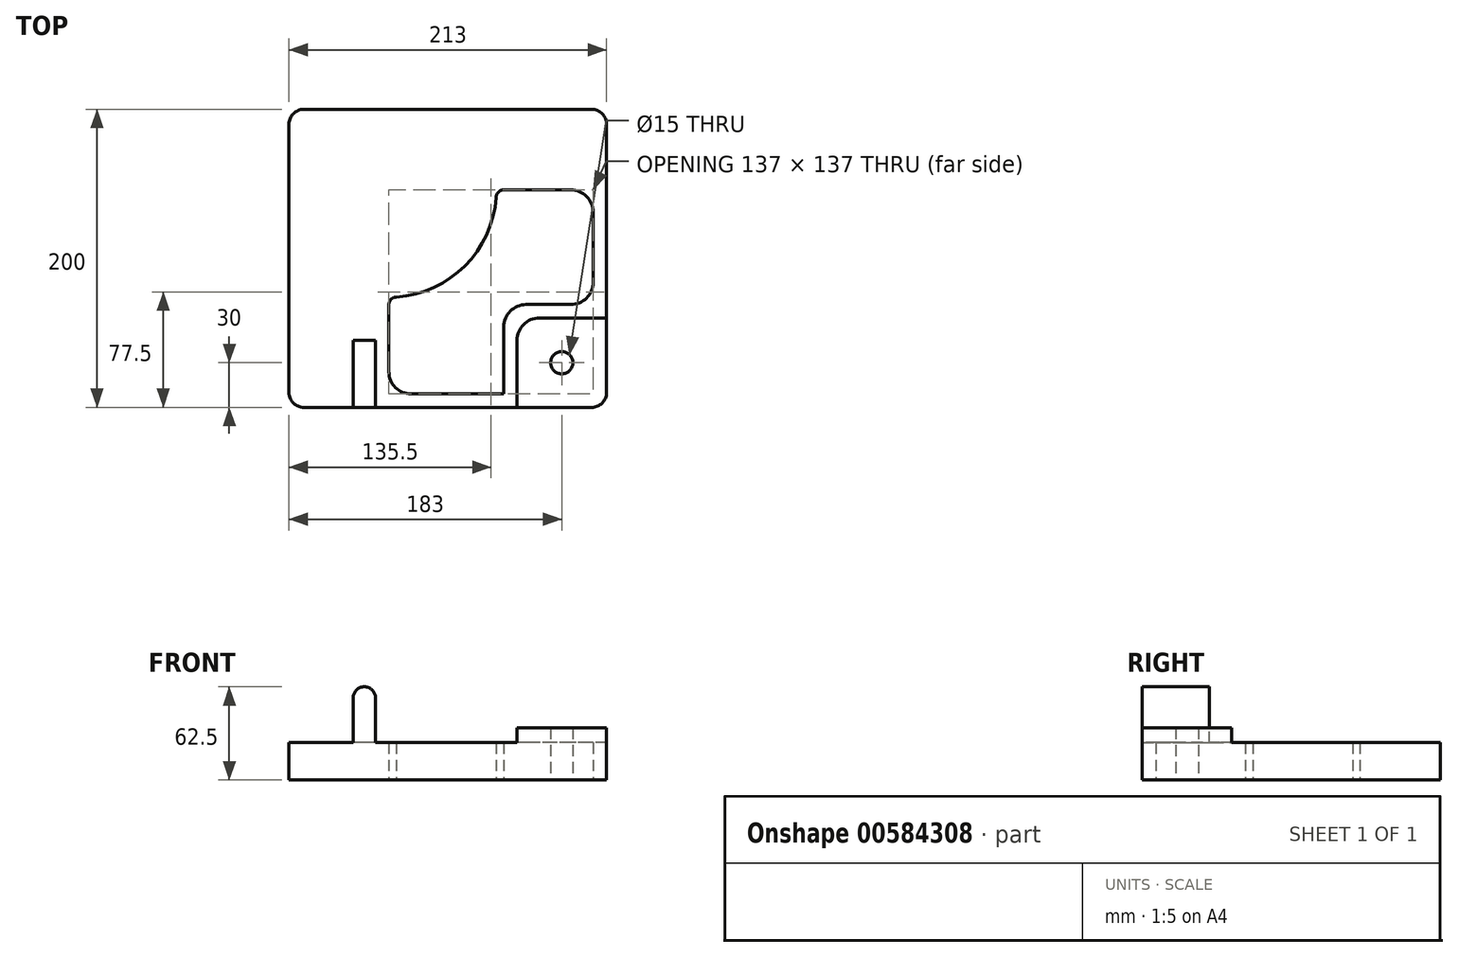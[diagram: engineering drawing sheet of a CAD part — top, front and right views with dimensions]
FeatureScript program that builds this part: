
annotation { "Feature Type Name" : "Feature", "Feature Type Description" : "" }
export const myFeature = defineFeature(function(context is Context, id is Id, definition is map)
    precondition{}
    {
        {
            var Q0;
            Q0=qCreatedBy(makeId("Top.planeOp"),FACE);
            var sketch = newSketch(context, id + "F0", { "sketchPlane" : qUnion([Q0])});
            skLineSegment(sketch, "E0.bottom", {"start": v(106.5, 100) * mm, "end": v(-106.5, 100) * mm});
            skLineSegment(sketch, "E0.top", {"start": v(106.5, -100) * mm, "end": v(-106.5, -100) * mm});
            skLineSegment(sketch, "E0.left", {"start": v(106.5, 100) * mm, "end": v(106.5, -100) * mm});
            skLineSegment(sketch, "E0.right", {"start": v(-106.5, 100) * mm, "end": v(-106.5, -100) * mm});
            skPoint(sketch, "E0.middle", {"position": v(0, 0) * mm});
            skLineSegment(sketch, "E1", {"start": v(106.5, -100) * mm, "end": v(-39.5, -100) * mm, "construction": true});
            skLineSegment(sketch, "E2", {"start": v(-39.5, -100) * mm, "end": v(-39.5, -91) * mm, "construction": true});
            skLineSegment(sketch, "E3", {"start": v(106.5, -100) * mm, "end": v(46.5, -100) * mm, "construction": true});
            skLineSegment(sketch, "E4", {"start": v(46.5, -100) * mm, "end": v(46.5, -40) * mm, "construction": true});
            skLineSegment(sketch, "E5", {"start": v(46.5, -40) * mm, "end": v(106.5, -40) * mm, "construction": true});
            skLineSegment(sketch, "E6", {"start": v(106.5, -40) * mm, "end": v(106.5, -100) * mm, "construction": true});
            skLineSegment(sketch, "E7", {"start": v(46.5, -40) * mm, "end": v(37.5, -40) * mm, "construction": true});
            skLineSegment(sketch, "E8", {"start": v(46.5, -40) * mm, "end": v(46.5, 46) * mm, "construction": true});
            skLineSegment(sketch, "E9", {"start": v(97.5, 46) * mm, "end": v(97.5, -16) * mm});
            skLineSegment(sketch, "E10", {"start": v(37.5, -91) * mm, "end": v(37.5, -46) * mm});
            skLineSegment(sketch, "E11", {"start": v(82.5, -31) * mm, "end": v(52.5, -31) * mm});
            skArc(sketch, "E12", {"start": v(37.5, -46) * mm, "mid": v(41.9, -35.4) * mm, "end": v(52.5, -31) * mm});
            skLineSegment(sketch, "E13", {"start": v(-39.5, -91) * mm, "end": v(37.5, -91) * mm});
            skLineSegment(sketch, "E14", {"start": v(97.5, 46) * mm, "end": v(82.5, 46) * mm});
            skLineSegment(sketch, "E15", {"start": v(97.5, 46) * mm, "end": v(97.5, 31) * mm});
            skLineSegment(sketch, "E16", {"start": v(97.5, 31) * mm, "end": v(82.5, 31) * mm, "construction": true});
            skLineSegment(sketch, "E17", {"start": v(82.5, 31) * mm, "end": v(82.5, 46) * mm, "construction": true});
            skLineSegment(sketch, "E18", {"start": v(37.5, -91) * mm, "end": v(22.5, -91) * mm});
            skLineSegment(sketch, "E19", {"start": v(22.5, -91) * mm, "end": v(37.5, -91) * mm});
            skLineSegment(sketch, "E20", {"start": v(37.5, -76) * mm, "end": v(37.5, -91) * mm});
            skArc(sketch, "E21", {"start": v(97.5, 31) * mm, "mid": v(93.1, 41.6) * mm, "end": v(82.5, 46) * mm});
            skArc(sketch, "E22", {"start": v(82.5, -31) * mm, "mid": v(93.1, -26.6) * mm, "end": v(97.5, -16) * mm});
            skLineSegment(sketch, "E23", {"start": v(22.5, -91) * mm, "end": v(22.5, -76) * mm, "construction": true});
            skLineSegment(sketch, "E24", {"start": v(37.5, -76) * mm, "end": v(22.5, -76) * mm, "construction": true});
            skArc(sketch, "E25", {"start": v(22.5, -91) * mm, "mid": v(33.1, -86.6) * mm, "end": v(37.5, -76) * mm});
            skLineSegment(sketch, "E26", {"start": v(-24.5, -91) * mm, "end": v(-24.5, -76) * mm, "construction": true});
            skLineSegment(sketch, "E27", {"start": v(-24.5, -76) * mm, "end": v(-39.5, -76) * mm, "construction": true});
            skArc(sketch, "E28", {"start": v(-24.5, -91) * mm, "mid": v(-35.1, -86.6) * mm, "end": v(-39.5, -76) * mm});
            skLineSegment(sketch, "E29", {"start": v(37.5, -46) * mm, "end": v(52.5, -46) * mm, "construction": true});
            skLineSegment(sketch, "E30", {"start": v(97.5, -16) * mm, "end": v(106.5, -16) * mm, "construction": true});
            skLineSegment(sketch, "E31", {"start": v(37.5, -46) * mm, "end": v(37.5, -31) * mm, "construction": true});
            skLineSegment(sketch, "E32", {"start": v(52.5, -31) * mm, "end": v(37.5, -31) * mm, "construction": true});
            skLineSegment(sketch, "E33", {"start": v(82.5, -16) * mm, "end": v(97.5, -16) * mm, "construction": true});
            skLineSegment(sketch, "E34", {"start": v(97.5, -16) * mm, "end": v(97.5, -31) * mm, "construction": true});
            skLineSegment(sketch, "E35", {"start": v(97.5, -31) * mm, "end": v(82.5, -31) * mm, "construction": true});
            skLineSegment(sketch, "E36", {"start": v(82.5, -31) * mm, "end": v(82.5, -16) * mm, "construction": true});
            skPoint(sketch, "E37.endSnap0", {"position": v(90, 46) * mm});
            skLineSegment(sketch, "E38", {"start": v(-39.5, -76) * mm, "end": v(-39.5, -31) * mm});
            skLineSegment(sketch, "E39", {"start": v(-39.5, -31) * mm, "end": v(-34.5, -31) * mm, "construction": true});
            skLineSegment(sketch, "E40", {"start": v(-34.5, -31) * mm, "end": v(-34.5, -26) * mm, "construction": true});
            skLineSegment(sketch, "E41", {"start": v(-34.5, -26) * mm, "end": v(-39.5, -26) * mm, "construction": true});
            skLineSegment(sketch, "E42", {"start": v(-39.5, -26) * mm, "end": v(-39.5, -31) * mm, "construction": true});
            skLineSegment(sketch, "E43", {"start": v(82.5, 46) * mm, "end": v(37.5, 46) * mm});
            skLineSegment(sketch, "E44", {"start": v(37.5, 46) * mm, "end": v(32.5, 46) * mm, "construction": true});
            skLineSegment(sketch, "E45", {"start": v(32.5, 46) * mm, "end": v(32.5, 41) * mm, "construction": true});
            skLineSegment(sketch, "E46", {"start": v(32.5, 41) * mm, "end": v(37.5, 41) * mm, "construction": true});
            skLineSegment(sketch, "E47", {"start": v(37.5, 41) * mm, "end": v(37.5, 46) * mm, "construction": true});
            skArc(sketch, "E48", {"start": v(32.5, 41) * mm, "mid": v(33.96, 44.54) * mm, "end": v(37.5, 46) * mm});
            skArc(sketch, "E49", {"start": v(-34.5, -26) * mm, "mid": v(11.53, -5.03) * mm, "end": v(32.5, 41) * mm});
            skArc(sketch, "E50", {"start": v(-39.5, -31) * mm, "mid": v(-38.04, -27.46) * mm, "end": v(-34.5, -26) * mm});
            skSolve(sketch);
        }
        {
            var Q0;
            Q0 = qSketchRegion(id + "F0", true);
            var Q1;
            Q1=makeQuery(id+"F0.imprint","IMPRINT",FACE,{"disambiguationData":[TD([[makeQuery(id+"F0.imprint","IMPRINT",EDGE,{"derivedFrom":sQuery(id+"F0.wireOp",EDGE,"E19")}),1.0]])]});
            var Q2;
            Q2=makeQuery(id+"F0.imprint","IMPRINT",FACE,{"disambiguationData":[TD([[makeQuery(id+"F0.imprint","IMPRINT",EDGE,{"derivedFrom":sQuery(id+"F0.wireOp",EDGE,"E14")}),1.0]])]});
            var Q3;
            {var subQ0=sQuery(id+"F0.wireOp",EDGE,"E15");Q3=makeQuery(id+"F0.imprint","IMPRINT",FACE,{"disambiguationData":[TD([[makeQuery(id+"F0.imprint","IMPRINT",EDGE,{"derivedFrom":subQ0}),-1.0]])]});}
            extrude(context, id + "F1", {"entities" : qUnion([Q0, Q1, Q2, Q3]), "depth" : 25 * mm, "offsetDistance" : 25 * mm});
        }
        {
            var Q0;
            Q0=makeQuery(id+"F1.opExtrude","CAP_FACE",FACE,{"disambiguationData":[OSD([sQuery(id+"F0.wireOp",EDGE,"E0.bottom"),sQuery(id+"F0.wireOp",EDGE,"E0.top"),sQuery(id+"F0.wireOp",EDGE,"E0.left"),sQuery(id+"F0.wireOp",EDGE,"E0.right"),sQuery(id+"F0.wireOp",EDGE,"E9"),sQuery(id+"F0.wireOp",EDGE,"E10"),sQuery(id+"F0.wireOp",EDGE,"E11"),sQuery(id+"F0.wireOp",EDGE,"E12"),sQuery(id+"F0.wireOp",EDGE,"E13"),sQuery(id+"F0.wireOp",EDGE,"E21"),sQuery(id+"F0.wireOp",EDGE,"E22"),sQuery(id+"F0.wireOp",EDGE,"E25"),sQuery(id+"F0.wireOp",EDGE,"E28"),sQuery(id+"F0.wireOp",EDGE,"341oGA3N-QfVs-hJU4-bRWz-pwT9450Hi9rS"),sQuery(id+"F0.wireOp",EDGE,"hwp4x6K8-EjHO-V7wA-SaIZ-Agrq0EeERVsK"),sQuery(id+"F0.wireOp",EDGE,"Q021tWxJ-XWci-jYhW-sqWL-JB7nNTNh4coq")])],"isStart":false});
            var sketch = newSketch(context, id + "F2", { "sketchPlane" : qUnion([Q0])});
            skLineSegment(sketch, "E51", {"start": v(106.5, -100) * mm, "end": v(46.5, -100) * mm});
            skLineSegment(sketch, "E52", {"start": v(106.5, -100) * mm, "end": v(106.5, -40) * mm});
            skLineSegment(sketch, "E53", {"start": v(106.5, -40) * mm, "end": v(46.5, -40) * mm});
            skLineSegment(sketch, "E54", {"start": v(46.5, -40) * mm, "end": v(46.5, -100) * mm});
            skLineSegment(sketch, "E55", {"start": v(46.5, -40) * mm, "end": v(46.5, -55) * mm, "construction": true});
            skLineSegment(sketch, "E56", {"start": v(46.5, -55) * mm, "end": v(61.5, -55) * mm, "construction": true});
            skLineSegment(sketch, "E57", {"start": v(61.5, -55) * mm, "end": v(61.5, -40) * mm, "construction": true});
            skLineSegment(sketch, "E58", {"start": v(61.5, -40) * mm, "end": v(46.5, -40) * mm, "construction": true});
            skArc(sketch, "E59", {"start": v(61.5, -40) * mm, "mid": v(50.9, -44.4) * mm, "end": v(46.5, -55) * mm});
            skLineSegment(sketch, "E60", {"start": v(106.5, -100) * mm, "end": v(76.5, -100) * mm, "construction": true});
            skLineSegment(sketch, "E61", {"start": v(76.5, -100) * mm, "end": v(76.5, -70) * mm, "construction": true});
            skCircle(sketch, "E62", {"center": v(76.5, -70) * mm, "radius": 7.5 * mm});
            skSolve(sketch);
        }
        {
            var Q0;
            {var subQ4=sQuery(id+"F2.wireOp",EDGE,"E51");Q0=makeQuery(id+"F2.imprint","IMPRINT",FACE,{"disambiguationData":[TD([[makeQuery(id+"F2.imprint","IMPRINT",EDGE,{"derivedFrom":subQ4}),-1.0]])]});}
            extrude(context, id + "F3", {"entities" : qUnion([Q0]), "operationType" : NewBodyOperationType.ADD, "depth" : 10 * mm, "offsetDistance" : 25 * mm});
        }
        {
            var Q0;
            Q0=makeQuery(id+"F3.boolean.opBoolean","SPLIT",FACE,{"disambiguationData":[TD([makeQuery(id+"F3.opExtrude","SWEPT_FACE",FACE,{"disambiguationData":[OSD([sQuery(id+"F2.wireOp",EDGE,"E62")])]})])],"derivedFrom":makeQuery(id+"F1.opExtrude","CAP_FACE",FACE,{"disambiguationData":[OSD([sQuery(id+"F0.wireOp",EDGE,"E0.bottom"),sQuery(id+"F0.wireOp",EDGE,"E0.top"),sQuery(id+"F0.wireOp",EDGE,"E0.left"),sQuery(id+"F0.wireOp",EDGE,"E0.right"),sQuery(id+"F0.wireOp",EDGE,"E9"),sQuery(id+"F0.wireOp",EDGE,"E10"),sQuery(id+"F0.wireOp",EDGE,"E11"),sQuery(id+"F0.wireOp",EDGE,"E12"),sQuery(id+"F0.wireOp",EDGE,"E13"),sQuery(id+"F0.wireOp",EDGE,"E21"),sQuery(id+"F0.wireOp",EDGE,"E22"),sQuery(id+"F0.wireOp",EDGE,"E25"),sQuery(id+"F0.wireOp",EDGE,"E28"),sQuery(id+"F0.wireOp",EDGE,"341oGA3N-QfVs-hJU4-bRWz-pwT9450Hi9rS"),sQuery(id+"F0.wireOp",EDGE,"hwp4x6K8-EjHO-V7wA-SaIZ-Agrq0EeERVsK"),sQuery(id+"F0.wireOp",EDGE,"Q021tWxJ-XWci-jYhW-sqWL-JB7nNTNh4coq")])],"isStart":false})});
            extrude(context, id + "F4", {"entities" : qUnion([Q0]), "operationType" : NewBodyOperationType.REMOVE, "oppositeDirection" : true, "depth" : 25 * mm, "offsetDistance" : 25 * mm});
        }
        {
            var Q0;
            Q0=makeQuery(id+"F3.boolean.opBoolean","MERGE",FACE,{"derivedFrom":[makeQuery(id+"F1.opExtrude","SWEPT_FACE",FACE,{"disambiguationData":[OSD([sQuery(id+"F0.wireOp",EDGE,"E0.top")])]}),makeQuery(id+"F3.opExtrude","SWEPT_FACE",FACE,{"disambiguationData":[OSD([sQuery(id+"F2.wireOp",EDGE,"E51")])]})]});
            var sketch = newSketch(context, id + "F5", { "sketchPlane" : qUnion([Q0])});
            skLineSegment(sketch, "E63", {"start": v(106.5, 25) * mm, "end": v(-63.5, 25) * mm, "construction": true});
            skLineSegment(sketch, "E64", {"start": v(-63.5, 25) * mm, "end": v(-63.5, 55) * mm});
            skLineSegment(sketch, "E65", {"start": v(-63.5, 25) * mm, "end": v(-48.5, 25) * mm, "construction": true});
            skLineSegment(sketch, "E66", {"start": v(-48.5, 25) * mm, "end": v(-48.5, 55) * mm});
            skArc(sketch, "E67", {"start": v(-63.5, 55) * mm, "mid": v(-56, 62.5) * mm, "end": v(-48.5, 55) * mm});
            skSolve(sketch);
        }
        {
            var Q0;
            Q0=makeQuery(id+"F1.opExtrude","SWEPT_EDGE",EDGE,{"disambiguationData":[OSD([sQuery(id+"F0.wireOp",EDGE,"E0.bottom"),sQuery(id+"F0.wireOp",EDGE,"E0.right")])]});
            var Q1;
            Q1=makeQuery(id+"F1.opExtrude","SWEPT_EDGE",EDGE,{"disambiguationData":[OSD([sQuery(id+"F0.wireOp",EDGE,"E0.bottom"),sQuery(id+"F0.wireOp",EDGE,"E0.left")])]});
            var Q2;
            Q2=makeQuery(id+"F3.boolean.opBoolean","MERGE",EDGE,{"derivedFrom":[makeQuery(id+"F1.opExtrude","SWEPT_EDGE",EDGE,{"disambiguationData":[OSD([sQuery(id+"F0.wireOp",EDGE,"E0.top"),sQuery(id+"F0.wireOp",EDGE,"E0.left")])]}),makeQuery(id+"F3.opExtrude","SWEPT_EDGE",EDGE,{"disambiguationData":[OSD([sQuery(id+"F2.wireOp",EDGE,"E51"),sQuery(id+"F2.wireOp",EDGE,"E52")])]})]});
            var Q3;
            Q3=makeQuery(id+"F1.opExtrude","SWEPT_EDGE",EDGE,{"disambiguationData":[OSD([sQuery(id+"F0.wireOp",EDGE,"E0.top"),sQuery(id+"F0.wireOp",EDGE,"E0.right")])]});
            fillet(context, id + "F6", {"entities" : qUnion([Q0, Q1, Q2, Q3]), "radius" : 10 * mm, "tangentPropagation" : true, "allowEdgeOverflow" : false});
        }
        {
            var Q0;
            {var subQ0=sQuery(id+"F5.wireOp",EDGE,"E64");Q0=makeQuery(id+"F5.imprint","IMPRINT",FACE,{"disambiguationData":[TD([[makeQuery(id+"F5.imprint","IMPRINT",EDGE,{"derivedFrom":subQ0}),-1.0]])]});}
            var Q1;
            Q1=makeQuery(id+"F1.opExtrude","CAP_EDGE",EDGE,{"disambiguationData":[OSD([sQuery(id+"F0.wireOp",EDGE,"E38")])],"isStart":false});
            sweep(context, id + "F7", {"operationType" : NewBodyOperationType.ADD, "profiles" : qUnion([Q0]), "path" : qUnion([Q1])});
        }
    });
